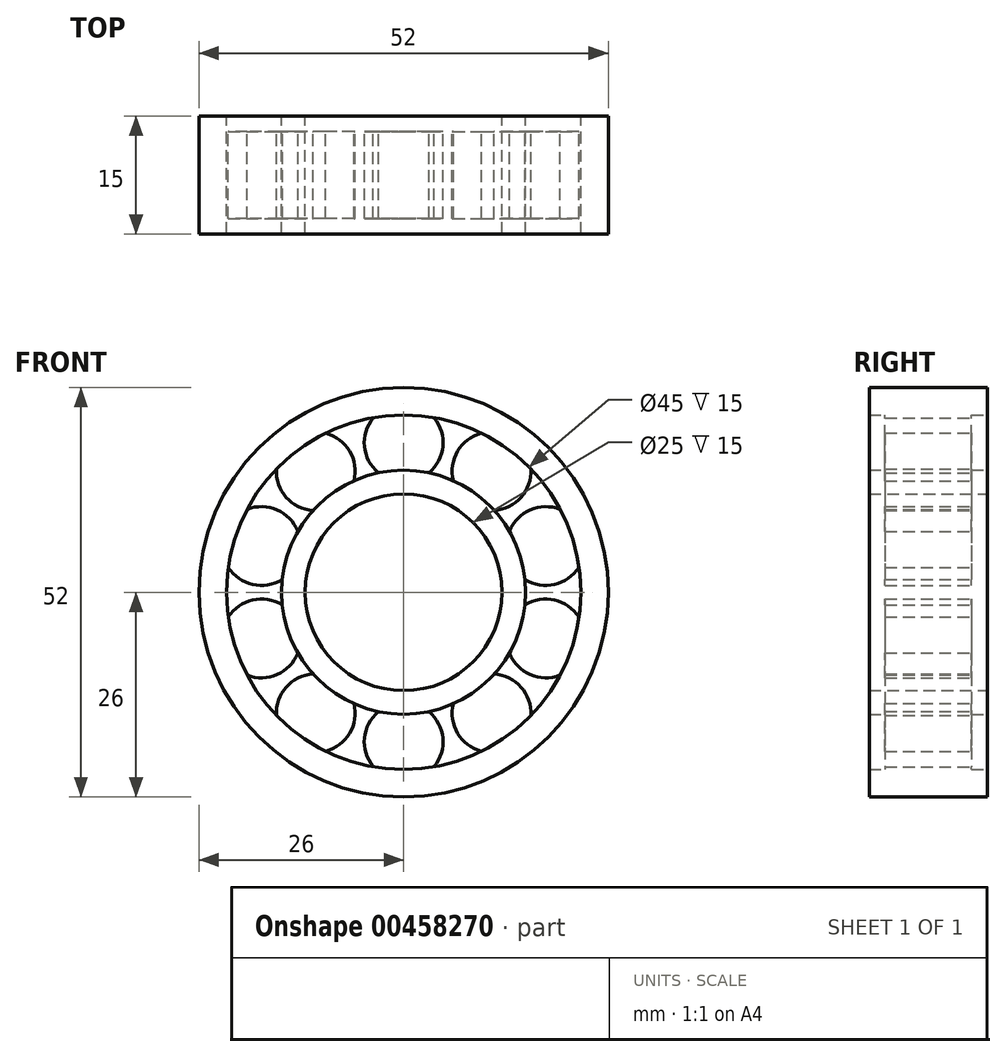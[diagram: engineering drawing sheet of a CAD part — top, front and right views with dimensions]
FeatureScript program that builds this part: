
annotation { "Feature Type Name" : "Feature", "Feature Type Description" : "" }
export const myFeature = defineFeature(function(context is Context, id is Id, definition is map)
    precondition{}
    {
        {
            var Q0;
            Q0=qCreatedBy(makeId("Front.planeOp"),FACE);
            cPlane(context, id + "F0", {"entities" : qUnion([Q0]), "cplaneType" : CPlaneType.OFFSET, "offset" : 7.5 * mm, "width" : 150 * mm, "height" : 150 * mm});
        }
        {
            var Q0;
            Q0=qCreatedBy(makeId("Front.planeOp"),FACE);
            var sketch = newSketch(context, id + "F1", { "sketchPlane" : qUnion([Q0])});
            skCircle(sketch, "E0", {"center": v(0, 0) * mm, "radius": 12.5 * mm});
            skCircle(sketch, "E1", {"center": v(0, 0) * mm, "radius": 15.5 * mm});
            skSolve(sketch);
        }
        {
            var Q0;
            Q0=qCreatedBy(makeId("Front.planeOp"),FACE);
            var sketch = newSketch(context, id + "F2", { "sketchPlane" : qUnion([Q0])});
            skCircle(sketch, "E2", {"center": v(0, 0) * mm, "radius": 22.5 * mm});
            skCircle(sketch, "E3", {"center": v(0, 0) * mm, "radius": 26 * mm});
            skSolve(sketch);
        }
        {
            var Q0;
            Q0=makeQuery(id+"F2.imprint","IMPRINT",FACE,{"disambiguationData":[TD([[makeQuery(id+"F2.imprint","IMPRINT",EDGE,{"derivedFrom":sQuery(id+"F2.wireOp",EDGE,"E2")}),-1.0]])]});
            extrude(context, id + "F3", {"entities" : qUnion([Q0]), "depth" : 15 * mm});
        }
        {
            var Q0;
            Q0 = qSketchRegion(id + "F1", true);
            extrude(context, id + "F4", {"entities" : qUnion([Q0]), "operationType" : NewBodyOperationType.ADD, "depth" : 15 * mm, "offsetDistance" : 25 * mm});
        }
        {
            var Q0;
            Q0=qCreatedBy(id+"F0.planeOp",FACE);
            var sketch = newSketch(context, id + "F5", { "sketchPlane" : qUnion([Q0])});
            skCircle(sketch, "E4", {"center": v(0, 0) * mm, "radius": 19 * mm});
            skCircle(sketch, "E5", {"center": v(0, 19) * mm, "radius": 5 * mm});
            skCircle(sketch, "E6.1.1", {"center": v(-11.17, 15.37) * mm, "radius": 5 * mm});
            skCircle(sketch, "E6.2.1", {"center": v(-18.07, 5.87) * mm, "radius": 5 * mm});
            skCircle(sketch, "E6.3.1", {"center": v(-18.07, -5.87) * mm, "radius": 5 * mm});
            skCircle(sketch, "E6.4.1", {"center": v(-11.17, -15.37) * mm, "radius": 5 * mm});
            skCircle(sketch, "E6.5.1", {"center": v(0, -19) * mm, "radius": 5 * mm});
            skCircle(sketch, "E6.6.1", {"center": v(11.17, -15.37) * mm, "radius": 5 * mm});
            skCircle(sketch, "E6.7.1", {"center": v(18.07, -5.87) * mm, "radius": 5 * mm});
            skCircle(sketch, "E6.8.1", {"center": v(18.07, 5.87) * mm, "radius": 5 * mm});
            skCircle(sketch, "E6.9.1", {"center": v(11.17, 15.37) * mm, "radius": 5 * mm});
            skSolve(sketch);
        }
        {
            var Q0;
            {var subQ0=sQuery(id+"F5.wireOp",EDGE,"E4");var subQ1=sQuery(id+"F5.wireOp",EDGE,"E6.2.1");var subQ2=makeQuery(id+"F5.imprint","INTERSECT",VERTEX,{"disambiguationData":[OD(0.0)],"derivedFrom":[subQ1,subQ0]});Q0=makeQuery(id+"F5.imprint","IMPRINT",FACE,{"disambiguationData":[TD([[makeQuery(id+"F5.imprint","IMPRINT",EDGE,{"disambiguationData":[TD([[subQ2,-1.0]])],"derivedFrom":subQ1}),1.0]])]});}
            var Q1;
            {var subQ0=sQuery(id+"F5.wireOp",EDGE,"E4");var subQ1=sQuery(id+"F5.wireOp",EDGE,"E6.2.1");var subQ2=makeQuery(id+"F5.imprint","INTERSECT",VERTEX,{"disambiguationData":[OD(0.0)],"derivedFrom":[subQ1,subQ0]});Q1=makeQuery(id+"F5.imprint","IMPRINT",FACE,{"disambiguationData":[TD([[makeQuery(id+"F5.imprint","IMPRINT",EDGE,{"disambiguationData":[TD([[subQ2,1.0]])],"derivedFrom":subQ1}),1.0]])]});}
            var Q2;
            {var subQ0=sQuery(id+"F5.wireOp",EDGE,"E4");var subQ1=sQuery(id+"F5.wireOp",EDGE,"E6.3.1");var subQ2=makeQuery(id+"F5.imprint","INTERSECT",VERTEX,{"disambiguationData":[OD(0.0)],"derivedFrom":[subQ1,subQ0]});Q2=makeQuery(id+"F5.imprint","IMPRINT",FACE,{"disambiguationData":[TD([[makeQuery(id+"F5.imprint","IMPRINT",EDGE,{"disambiguationData":[TD([[subQ2,-1.0]])],"derivedFrom":subQ1}),1.0]])]});}
            var Q3;
            {var subQ0=sQuery(id+"F5.wireOp",EDGE,"E4");var subQ1=sQuery(id+"F5.wireOp",EDGE,"E6.3.1");var subQ2=makeQuery(id+"F5.imprint","INTERSECT",VERTEX,{"disambiguationData":[OD(0.0)],"derivedFrom":[subQ1,subQ0]});Q3=makeQuery(id+"F5.imprint","IMPRINT",FACE,{"disambiguationData":[TD([[makeQuery(id+"F5.imprint","IMPRINT",EDGE,{"disambiguationData":[TD([[subQ2,1.0]])],"derivedFrom":subQ1}),1.0]])]});}
            var Q4;
            {var subQ0=sQuery(id+"F5.wireOp",EDGE,"E4");var subQ1=sQuery(id+"F5.wireOp",EDGE,"E6.4.1");var subQ2=makeQuery(id+"F5.imprint","INTERSECT",VERTEX,{"disambiguationData":[OD(0.0)],"derivedFrom":[subQ1,subQ0]});Q4=makeQuery(id+"F5.imprint","IMPRINT",FACE,{"disambiguationData":[TD([[makeQuery(id+"F5.imprint","IMPRINT",EDGE,{"disambiguationData":[TD([[subQ2,-1.0]])],"derivedFrom":subQ1}),1.0]])]});}
            var Q5;
            {var subQ0=sQuery(id+"F5.wireOp",EDGE,"E4");var subQ1=sQuery(id+"F5.wireOp",EDGE,"E6.4.1");var subQ2=makeQuery(id+"F5.imprint","INTERSECT",VERTEX,{"disambiguationData":[OD(0.0)],"derivedFrom":[subQ1,subQ0]});Q5=makeQuery(id+"F5.imprint","IMPRINT",FACE,{"disambiguationData":[TD([[makeQuery(id+"F5.imprint","IMPRINT",EDGE,{"disambiguationData":[TD([[subQ2,1.0]])],"derivedFrom":subQ1}),1.0]])]});}
            var Q6;
            {var subQ0=sQuery(id+"F5.wireOp",EDGE,"E4");var subQ1=sQuery(id+"F5.wireOp",EDGE,"E6.5.1");var subQ2=makeQuery(id+"F5.imprint","INTERSECT",VERTEX,{"disambiguationData":[OD(0.0)],"derivedFrom":[subQ1,subQ0]});Q6=makeQuery(id+"F5.imprint","IMPRINT",FACE,{"disambiguationData":[TD([[makeQuery(id+"F5.imprint","IMPRINT",EDGE,{"disambiguationData":[TD([[subQ2,1.0]])],"derivedFrom":subQ1}),1.0]])]});}
            var Q7;
            {var subQ0=sQuery(id+"F5.wireOp",EDGE,"E4");var subQ1=sQuery(id+"F5.wireOp",EDGE,"E6.5.1");var subQ2=makeQuery(id+"F5.imprint","INTERSECT",VERTEX,{"disambiguationData":[OD(0.0)],"derivedFrom":[subQ1,subQ0]});Q7=makeQuery(id+"F5.imprint","IMPRINT",FACE,{"disambiguationData":[TD([[makeQuery(id+"F5.imprint","IMPRINT",EDGE,{"disambiguationData":[TD([[subQ2,-1.0]])],"derivedFrom":subQ1}),1.0]])]});}
            var Q8;
            {var subQ0=sQuery(id+"F5.wireOp",EDGE,"E4");var subQ1=sQuery(id+"F5.wireOp",EDGE,"E6.6.1");var subQ2=makeQuery(id+"F5.imprint","INTERSECT",VERTEX,{"disambiguationData":[OD(0.0)],"derivedFrom":[subQ1,subQ0]});Q8=makeQuery(id+"F5.imprint","IMPRINT",FACE,{"disambiguationData":[TD([[makeQuery(id+"F5.imprint","IMPRINT",EDGE,{"disambiguationData":[TD([[subQ2,-1.0]])],"derivedFrom":subQ1}),1.0]])]});}
            var Q9;
            {var subQ0=sQuery(id+"F5.wireOp",EDGE,"E4");var subQ1=sQuery(id+"F5.wireOp",EDGE,"E6.6.1");var subQ2=makeQuery(id+"F5.imprint","INTERSECT",VERTEX,{"disambiguationData":[OD(0.0)],"derivedFrom":[subQ1,subQ0]});Q9=makeQuery(id+"F5.imprint","IMPRINT",FACE,{"disambiguationData":[TD([[makeQuery(id+"F5.imprint","IMPRINT",EDGE,{"disambiguationData":[TD([[subQ2,1.0]])],"derivedFrom":subQ1}),1.0]])]});}
            var Q10;
            {var subQ0=sQuery(id+"F5.wireOp",EDGE,"E4");var subQ1=sQuery(id+"F5.wireOp",EDGE,"E6.7.1");var subQ2=makeQuery(id+"F5.imprint","INTERSECT",VERTEX,{"disambiguationData":[OD(0.0)],"derivedFrom":[subQ1,subQ0]});Q10=makeQuery(id+"F5.imprint","IMPRINT",FACE,{"disambiguationData":[TD([[makeQuery(id+"F5.imprint","IMPRINT",EDGE,{"disambiguationData":[TD([[subQ2,-1.0]])],"derivedFrom":subQ1}),1.0]])]});}
            var Q11;
            {var subQ0=sQuery(id+"F5.wireOp",EDGE,"E4");var subQ1=sQuery(id+"F5.wireOp",EDGE,"E6.7.1");var subQ2=makeQuery(id+"F5.imprint","INTERSECT",VERTEX,{"disambiguationData":[OD(0.0)],"derivedFrom":[subQ1,subQ0]});Q11=makeQuery(id+"F5.imprint","IMPRINT",FACE,{"disambiguationData":[TD([[makeQuery(id+"F5.imprint","IMPRINT",EDGE,{"disambiguationData":[TD([[subQ2,1.0]])],"derivedFrom":subQ1}),1.0]])]});}
            var Q12;
            {var subQ0=sQuery(id+"F5.wireOp",EDGE,"E4");var subQ1=sQuery(id+"F5.wireOp",EDGE,"E6.8.1");var subQ2=makeQuery(id+"F5.imprint","INTERSECT",VERTEX,{"disambiguationData":[OD(0.0)],"derivedFrom":[subQ1,subQ0]});Q12=makeQuery(id+"F5.imprint","IMPRINT",FACE,{"disambiguationData":[TD([[makeQuery(id+"F5.imprint","IMPRINT",EDGE,{"disambiguationData":[TD([[subQ2,-1.0]])],"derivedFrom":subQ1}),1.0]])]});}
            var Q13;
            {var subQ0=sQuery(id+"F5.wireOp",EDGE,"E4");var subQ1=sQuery(id+"F5.wireOp",EDGE,"E6.8.1");var subQ2=makeQuery(id+"F5.imprint","INTERSECT",VERTEX,{"disambiguationData":[OD(0.0)],"derivedFrom":[subQ1,subQ0]});Q13=makeQuery(id+"F5.imprint","IMPRINT",FACE,{"disambiguationData":[TD([[makeQuery(id+"F5.imprint","IMPRINT",EDGE,{"disambiguationData":[TD([[subQ2,1.0]])],"derivedFrom":subQ1}),1.0]])]});}
            var Q14;
            {var subQ0=sQuery(id+"F5.wireOp",EDGE,"E6.9.1");var subQ1=sQuery(id+"F5.wireOp",EDGE,"E4");var subQ2=makeQuery(id+"F5.imprint","INTERSECT",VERTEX,{"disambiguationData":[OD(0.0)],"derivedFrom":[subQ1,subQ0]});Q14=makeQuery(id+"F5.imprint","IMPRINT",FACE,{"disambiguationData":[TD([[makeQuery(id+"F5.imprint","IMPRINT",EDGE,{"disambiguationData":[TD([[subQ2,-1.0]])],"derivedFrom":subQ1}),1.0]])]});}
            var Q15;
            {var subQ0=sQuery(id+"F5.wireOp",EDGE,"E6.9.1");var subQ1=sQuery(id+"F5.wireOp",EDGE,"E4");var subQ2=makeQuery(id+"F5.imprint","INTERSECT",VERTEX,{"disambiguationData":[OD(0.0)],"derivedFrom":[subQ1,subQ0]});Q15=makeQuery(id+"F5.imprint","IMPRINT",FACE,{"disambiguationData":[TD([[makeQuery(id+"F5.imprint","IMPRINT",EDGE,{"disambiguationData":[TD([[subQ2,-1.0]])],"derivedFrom":subQ1}),-1.0]])]});}
            var Q16;
            {var subQ0=sQuery(id+"F5.wireOp",EDGE,"E4");var subQ1=sQuery(id+"F5.wireOp",EDGE,"E5");var subQ2=makeQuery(id+"F5.imprint","INTERSECT",VERTEX,{"disambiguationData":[OD(0.0)],"derivedFrom":[subQ1,subQ0]});Q16=makeQuery(id+"F5.imprint","IMPRINT",FACE,{"disambiguationData":[TD([[makeQuery(id+"F5.imprint","IMPRINT",EDGE,{"disambiguationData":[TD([[subQ2,1.0]])],"derivedFrom":subQ1}),1.0]])]});}
            var Q17;
            {var subQ0=sQuery(id+"F5.wireOp",EDGE,"E4");var subQ1=sQuery(id+"F5.wireOp",EDGE,"E5");var subQ2=makeQuery(id+"F5.imprint","INTERSECT",VERTEX,{"disambiguationData":[OD(0.0)],"derivedFrom":[subQ1,subQ0]});Q17=makeQuery(id+"F5.imprint","IMPRINT",FACE,{"disambiguationData":[TD([[makeQuery(id+"F5.imprint","IMPRINT",EDGE,{"disambiguationData":[TD([[subQ2,-1.0]])],"derivedFrom":subQ1}),1.0]])]});}
            var Q18;
            {var subQ0=sQuery(id+"F5.wireOp",EDGE,"E4");var subQ1=sQuery(id+"F5.wireOp",EDGE,"E6.1.1");var subQ2=makeQuery(id+"F5.imprint","INTERSECT",VERTEX,{"disambiguationData":[OD(0.0)],"derivedFrom":[subQ1,subQ0]});Q18=makeQuery(id+"F5.imprint","IMPRINT",FACE,{"disambiguationData":[TD([[makeQuery(id+"F5.imprint","IMPRINT",EDGE,{"disambiguationData":[TD([[subQ2,1.0]])],"derivedFrom":subQ1}),1.0]])]});}
            var Q19;
            {var subQ0=sQuery(id+"F5.wireOp",EDGE,"E4");var subQ1=sQuery(id+"F5.wireOp",EDGE,"E6.1.1");var subQ2=makeQuery(id+"F5.imprint","INTERSECT",VERTEX,{"disambiguationData":[OD(0.0)],"derivedFrom":[subQ1,subQ0]});Q19=makeQuery(id+"F5.imprint","IMPRINT",FACE,{"disambiguationData":[TD([[makeQuery(id+"F5.imprint","IMPRINT",EDGE,{"disambiguationData":[TD([[subQ2,-1.0]])],"derivedFrom":subQ1}),1.0]])]});}
            extrude(context, id + "F6", {"entities" : qUnion([Q0, Q1, Q2, Q3, Q4, Q5, Q6, Q7, Q8, Q9, Q10, Q11, Q12, Q13, Q14, Q15, Q16, Q17, Q18, Q19]), "operationType" : NewBodyOperationType.ADD, "depth" : 11 * mm, "offsetDistance" : 25 * mm, "symmetric" : true});
        }
    });
